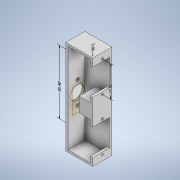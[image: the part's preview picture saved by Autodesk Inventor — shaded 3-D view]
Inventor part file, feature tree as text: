
AUTODESK INVENTOR PART (.ipt)
format: ipt  version: 2022.2 (Build 262287010, 287A)  size: 252,416 bytes
history: native  units: mm
features: extrude x11, sketch x10, other x6
ambient origin geometry x8: Origin, YZ Plane, XZ Plane, XY Plane, X Axis, Y Axis, Z Axis, Center Point
bodies: Solid1 (feature_tree)
feature tree (27):
  other  "Annotations"
  extrude  "Extrusion1"  Depth=80.0mm
  extrude  "Extrusion2"  Depth=2.0mm
  extrude  "Extrusion3"  Depth=15.0mm TaperAngle=0.0deg
  extrude  "Extrusion4"  Depth=2.0mm
  extrude  "Extrusion5"  Depth=8.5mm
  extrude  "Extrusion12"  Depth=3.0mm
  extrude  "Extrusion13"  Depth=23.5mm
  extrude  "Extrusion14"  Depth=5.0mm
  extrude  "Extrusion15"  Depth=5.0mm
  other  "Plano de trabalho3"
  extrude  "Extrusion18"  Depth=2.0mm TaperAngle=0.0deg
  extrude  "Extrusão19"  Depth=15.0mm
  sketch  "Sketch1"  dims[d0=24.0mm d1=80.0mm]
  sketch  "Sketch2"  dims[d2=2.0mm d3=0.0mm d4=2.0mm]
  sketch  "Sketch3"  dims[d5=2.0mm d6=15.0mm d7=0.0mm]
  sketch  "Sketch5"  dims[d8=2.0mm d9=2.0mm]
  sketch  "Sketch15"  dims[d10=8.5mm d11=8.5mm]
  sketch  "Sketch16"  dims[d12=27.5mm d13=3.0mm]
  sketch  "Sketch17"  dims[d14=12.0mm d15=0.0mm d24=23.5mm]
  sketch  "Sketch18"  dims[d27=15.0mm d28=0.0mm d29=5.0mm]
  sketch  "Sketch21"  dims[d30=5.0mm d31=0.0mm d32=8.6mm]
  sketch  "Esboço22"  dims[d33=0.0mm d70=2.0mm d71=0.0mm d84=15.0mm d85=23.5mm d86=5.0mm d87=2.0mm d88=2.0mm d89=8.5mm d90=8.5mm d91=2.0mm d92=2.0mm d93=2.0mm d94=0.0mm d95=2.0mm d96=0.0mm d97=5.0mm d98=13.6mm d99=8.5mm d100=5.0mm d101=0.0mm d104=15.0mm d105=2.0mm d106=2.0mm d122=12.0mm d124=8.5mm d125=10.0mm d126=0.0mm d129=3.0mm d130=3.0mm d131=10.0mm d132=10.0mm d134=40.0mm d142=10.0mm d143=5.0mm d144=5.0mm d145=10.0mm d146=0.0mm d110=56.8mm d78=4.776933mm d79=3.0mm d80=27.5mm d81=7.865088mm d82=1.505127mm d83=8.5mm]
  other  "Linear Dimension 6"
  other  "Linear Dimension 7"
  other  "Linear Dimension 8"
  other  "Linear Dimension 10"
